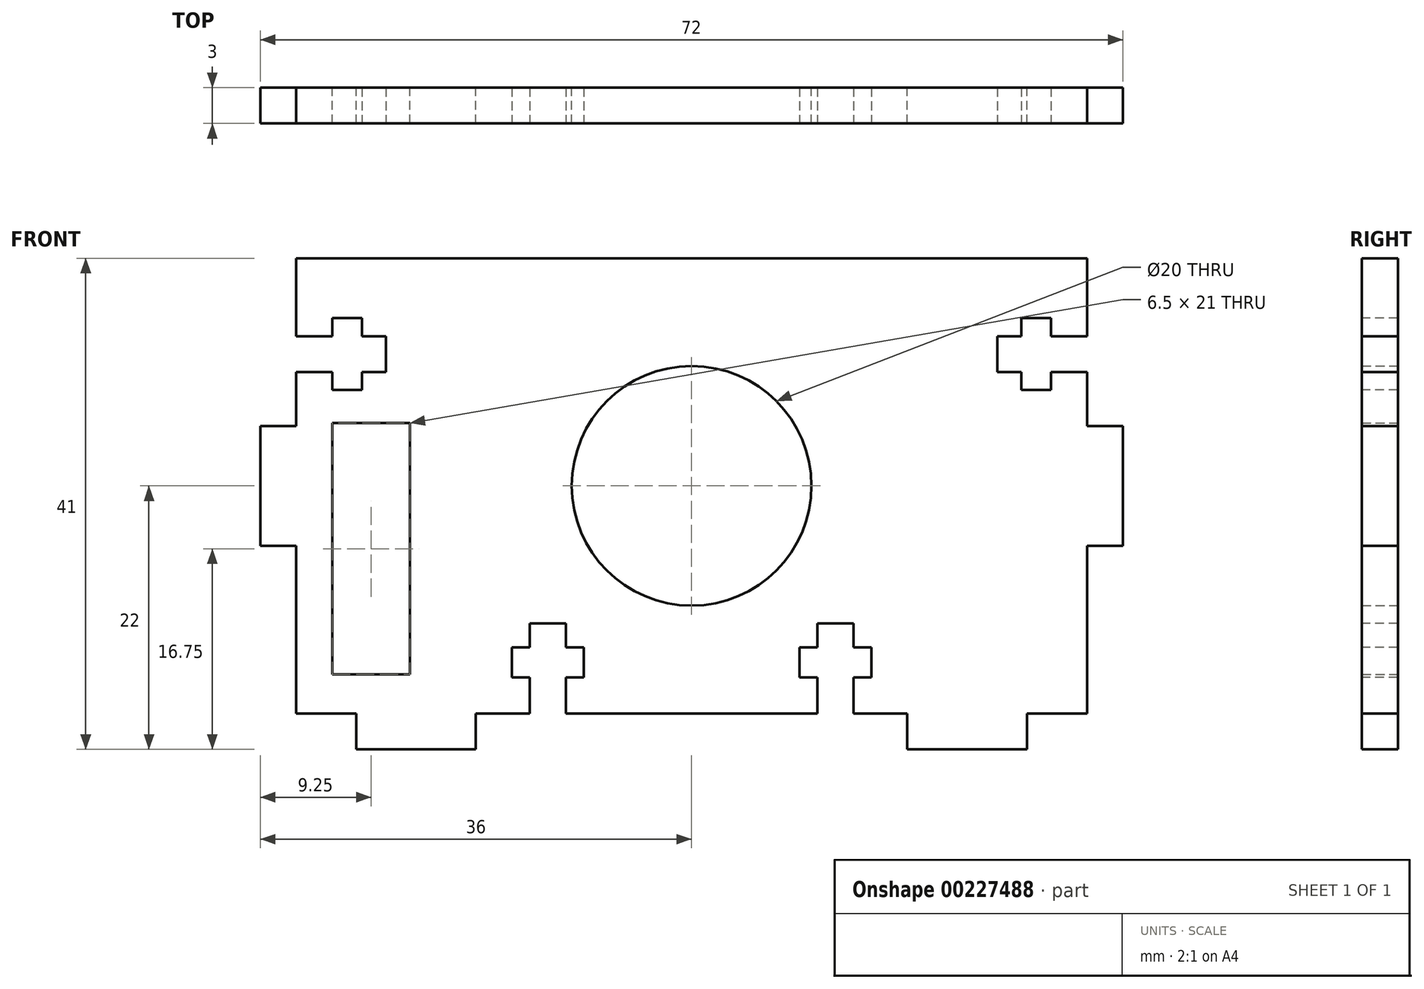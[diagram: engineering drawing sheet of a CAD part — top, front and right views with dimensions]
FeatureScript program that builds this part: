
annotation { "Feature Type Name" : "Feature", "Feature Type Description" : "" }
export const myFeature = defineFeature(function(context is Context, id is Id, definition is map)
    precondition{}
    {
        {
            var Q0;
            Q0=qCreatedBy(makeId("Front.planeOp"),FACE);
            var sketch = newSketch(context, id + "F0", { "sketchPlane" : qUnion([Q0])});
            skLineSegment(sketch, "E0.top", {"start": v(33, 19) * mm, "end": v(-33, 19) * mm});
            skPoint(sketch, "E0.middle", {"position": v(0, 0) * mm});
            skCircle(sketch, "E1", {"center": v(0, 0) * mm, "radius": 10 * mm});
            skPoint(sketch, "E2", {"position": v(0, 19) * mm});
            skLineSegment(sketch, "E3", {"start": v(-28, -19) * mm, "end": v(-28, -22) * mm});
            skLineSegment(sketch, "E4", {"start": v(-28, -22) * mm, "end": v(-18, -22) * mm});
            skLineSegment(sketch, "E5", {"start": v(-18, -22) * mm, "end": v(-18, -19) * mm});
            skLineSegment(sketch, "E6", {"start": v(-18, -19) * mm, "end": v(0, -19) * mm});
            skLineSegment(sketch, "E7.MirrorCS", {"start": v(18, -19) * mm, "end": v(0, -19) * mm});
            skLineSegment(sketch, "E8.MirrorCS", {"start": v(18, -22) * mm, "end": v(18, -19) * mm});
            skLineSegment(sketch, "E9.MirrorCS", {"start": v(28, -22) * mm, "end": v(18, -22) * mm});
            skLineSegment(sketch, "E10.MirrorCS", {"start": v(28, -19) * mm, "end": v(28, -22) * mm});
            skLineSegment(sketch, "E11", {"start": v(-33, -19) * mm, "end": v(-33, -5) * mm});
            skLineSegment(sketch, "E12", {"start": v(-33, -5) * mm, "end": v(-36, -5) * mm});
            skLineSegment(sketch, "E13", {"start": v(-36, -5) * mm, "end": v(-36, 5) * mm});
            skLineSegment(sketch, "E14", {"start": v(-36, 5) * mm, "end": v(-33, 5) * mm});
            skLineSegment(sketch, "E15", {"start": v(-33, 5) * mm, "end": v(-33, 19) * mm});
            skPoint(sketch, "E16", {"position": v(-36, 0) * mm});
            skLineSegment(sketch, "E17.MirrorCS", {"start": v(33, 5) * mm, "end": v(33, 19) * mm});
            skLineSegment(sketch, "E18.MirrorCS", {"start": v(36, 5) * mm, "end": v(33, 5) * mm});
            skLineSegment(sketch, "E19.MirrorCS", {"start": v(36, -5) * mm, "end": v(36, 5) * mm});
            skLineSegment(sketch, "E20.MirrorCS", {"start": v(33, -5) * mm, "end": v(36, -5) * mm});
            skLineSegment(sketch, "E21.MirrorCS", {"start": v(33, -19) * mm, "end": v(33, -5) * mm});
            skLineSegment(sketch, "E22", {"start": v(28, -19) * mm, "end": v(33, -19) * mm});
            skLineSegment(sketch, "E23", {"start": v(-28, -19) * mm, "end": v(-33, -19) * mm});
            skLineSegment(sketch, "E24.bottom", {"start": v(-30, 5.25) * mm, "end": v(-23.5, 5.25) * mm});
            skLineSegment(sketch, "E24.top", {"start": v(-30, -15.75) * mm, "end": v(-23.5, -15.75) * mm});
            skLineSegment(sketch, "E24.left", {"start": v(-30, 5.25) * mm, "end": v(-30, -15.75) * mm});
            skLineSegment(sketch, "E24.right", {"start": v(-23.5, 5.25) * mm, "end": v(-23.5, -15.75) * mm});
            skSolve(sketch);
        }
        {
            var Q0;
            Q0=makeQuery(id+"F0.imprint","IMPRINT",FACE,{"disambiguationData":[TD([[makeQuery(id+"F0.imprint","IMPRINT",EDGE,{"derivedFrom":sQuery(id+"F0.wireOp",EDGE,"E0.bottom")}),-1.0]])]});
            var Q1;
            Q1=makeQuery(id+"F0.imprint","IMPRINT",FACE,{"disambiguationData":[TD([[makeQuery(id+"F0.imprint","IMPRINT",EDGE,{"derivedFrom":sQuery(id+"F0.wireOp",EDGE,"E0.top")}),1.0]])]});
            extrude(context, id + "F1", {"entities" : qUnion([Q0, Q1]), "depth" : 3 * mm});
        }
        {
            var Q0;
            Q0=makeQuery(id+"F1.opExtrude","CAP_FACE",FACE,{"disambiguationData":[OSD([sQuery(id+"F0.wireOp",EDGE,"E0.top"),sQuery(id+"F0.wireOp",EDGE,"E1"),sQuery(id+"F0.wireOp",EDGE,"i2BJ4We7-Z1tz-6YYD-7Gnh-UwGsJDHukj4o"),sQuery(id+"F0.wireOp",EDGE,"H5TLaSxA-TAvm-WxYI-6s5p-rbUKsHJPtpz8"),sQuery(id+"F0.wireOp",EDGE,"fE5sAuBm-J1N4-LUQK-MxoP-oJGd3h4EWBky"),sQuery(id+"F0.wireOp",EDGE,"UVkaeSOW-HMeC-MlRq-fWxO-58zO0Vm4gzLd"),sQuery(id+"F0.wireOp",EDGE,"4oAcHBtJ-SWL1-Us38-5a5N-tiTYXxMsnVxl"),sQuery(id+"F0.wireOp",EDGE,"MGHFterx-abw6-INuc-nvHV-QaNsLm6ah1ng"),sQuery(id+"F0.wireOp",EDGE,"DztduCwT-NtgE-rZnK-mSEW-EnSqVKOmk10X"),sQuery(id+"F0.wireOp",EDGE,"XImseshz-UxQT-ogDy-5Lvy-O5B2oz8zv5fS"),sQuery(id+"F0.wireOp",EDGE,"FHz1HeJZ-Y50a-yfiC-Rnzm-b0fU7RSFoIpM"),sQuery(id+"F0.wireOp",EDGE,"bBcTDBjg-FDSx-XcTB-SbE1-9syf6QqrHLmC"),sQuery(id+"F0.wireOp",EDGE,"1vXtDNT1-yAZY-NYDk-InIM-wFA5S2rVquaF"),sQuery(id+"F0.wireOp",EDGE,"rcTIoJpC-EadT-N3WT-61kg-b3dVzh2UPf16"),sQuery(id+"F0.wireOp",EDGE,"V9EOst0m-YofT-ZeQ4-KXmd-etc1AHxpQRv2"),sQuery(id+"F0.wireOp",EDGE,"E3"),sQuery(id+"F0.wireOp",EDGE,"E4"),sQuery(id+"F0.wireOp",EDGE,"E5"),sQuery(id+"F0.wireOp",EDGE,"E6"),sQuery(id+"F0.wireOp",EDGE,"E7.MirrorCS"),sQuery(id+"F0.wireOp",EDGE,"E8.MirrorCS"),sQuery(id+"F0.wireOp",EDGE,"E9.MirrorCS"),sQuery(id+"F0.wireOp",EDGE,"E10.MirrorCS"),sQuery(id+"F0.wireOp",EDGE,"4fc586d0-1a2d-4033-9ad1-b4b14924f1e60.MirrorCS"),sQuery(id+"F0.wireOp",EDGE,"25921314-2feb-4960-9358-c6f40c29e8060.MirrorCS"),sQuery(id+"F0.wireOp",EDGE,"92609e8c-4cca-44cb-b192-d1e8ea80d6400.MirrorCS"),sQuery(id+"F0.wireOp",EDGE,"c6435143-3ef5-4a16-a53c-0c7a1f294e250.MirrorCS"),sQuery(id+"F0.wireOp",EDGE,"302a1fd6-7f51-4dcd-b85b-b87c70c5ff6f0.MirrorCS"),sQuery(id+"F0.wireOp",EDGE,"271ff51f-9e70-48b1-9ca4-6ffa4ba6ee090.MirrorCS"),sQuery(id+"F0.wireOp",EDGE,"7c8ad784-0027-4aca-88da-cb9512f49f770.MirrorCS"),sQuery(id+"F0.wireOp",EDGE,"aab8c399-5e78-4643-9a76-05bc1427fb740.MirrorCS"),sQuery(id+"F0.wireOp",EDGE,"2a5f69ab-9c37-4cf4-a27a-83d52b59f34f0.MirrorCS"),sQuery(id+"F0.wireOp",EDGE,"8a72d888-9ff6-4074-9ea7-52382edc54d80.MirrorCS"),sQuery(id+"F0.wireOp",EDGE,"2b144515-558f-4b7e-bfd9-8a7150f656b50.MirrorCS"),sQuery(id+"F0.wireOp",EDGE,"7271def4-b984-4847-8607-e135956054630.MirrorCS"),sQuery(id+"F0.wireOp",EDGE,"d1406031-9f0b-476a-854e-e83de3dd73970.MirrorCS"),sQuery(id+"F0.wireOp",EDGE,"0yL6zwbu-xF7a-lJXO-zZG0-wwet5oho1wIb"),sQuery(id+"F0.wireOp",EDGE,"46feee59-1b5a-4064-8cc5-d9cbb5a2c9400.MirrorC"),sQuery(id+"F0.wireOp",EDGE,"E11"),sQuery(id+"F0.wireOp",EDGE,"E12"),sQuery(id+"F0.wireOp",EDGE,"E13"),sQuery(id+"F0.wireOp",EDGE,"E14"),sQuery(id+"F0.wireOp",EDGE,"E15"),sQuery(id+"F0.wireOp",EDGE,"E17.MirrorCS"),sQuery(id+"F0.wireOp",EDGE,"E18.MirrorCS"),sQuery(id+"F0.wireOp",EDGE,"E19.MirrorCS"),sQuery(id+"F0.wireOp",EDGE,"E20.MirrorCS"),sQuery(id+"F0.wireOp",EDGE,"E21.MirrorCS")])],"isStart":false});
            var sketch = newSketch(context, id + "F2", { "sketchPlane" : qUnion([Q0])});
            skLineSegment(sketch, "E25", {"start": v(10.5, -19) * mm, "end": v(10.5, -16) * mm});
            skLineSegment(sketch, "E26", {"start": v(10.5, -16) * mm, "end": v(9, -16) * mm});
            skLineSegment(sketch, "E27", {"start": v(9, -16) * mm, "end": v(9, -13.5) * mm});
            skLineSegment(sketch, "E28", {"start": v(9, -13.5) * mm, "end": v(10.5, -13.5) * mm});
            skLineSegment(sketch, "E29", {"start": v(10.5, -13.5) * mm, "end": v(10.5, -11.5) * mm});
            skLineSegment(sketch, "E30", {"start": v(10.5, -11.5) * mm, "end": v(13.5, -11.5) * mm});
            skLineSegment(sketch, "E31", {"start": v(13.5, -11.5) * mm, "end": v(13.5, -13.5) * mm});
            skLineSegment(sketch, "E32", {"start": v(13.5, -13.5) * mm, "end": v(15, -13.5) * mm});
            skLineSegment(sketch, "E33", {"start": v(15, -13.5) * mm, "end": v(15, -16) * mm});
            skLineSegment(sketch, "E34", {"start": v(15, -16) * mm, "end": v(13.5, -16) * mm});
            skLineSegment(sketch, "E35", {"start": v(13.5, -16) * mm, "end": v(13.5, -19) * mm});
            skPoint(sketch, "E36", {"position": v(12, -19) * mm});
            skLineSegment(sketch, "E37", {"start": v(13.5, -19) * mm, "end": v(10.5, -19) * mm});
            skLineSegment(sketch, "E38", {"start": v(33, 9.5) * mm, "end": v(30, 9.5) * mm});
            skLineSegment(sketch, "E39", {"start": v(30, 9.5) * mm, "end": v(30, 8) * mm});
            skLineSegment(sketch, "E40", {"start": v(30, 8) * mm, "end": v(27.5, 8) * mm});
            skLineSegment(sketch, "E41", {"start": v(27.5, 8) * mm, "end": v(27.5, 9.5) * mm});
            skLineSegment(sketch, "E42", {"start": v(27.5, 9.5) * mm, "end": v(25.5, 9.5) * mm});
            skLineSegment(sketch, "E43", {"start": v(25.5, 9.5) * mm, "end": v(25.5, 12.5) * mm});
            skLineSegment(sketch, "E44", {"start": v(25.5, 12.5) * mm, "end": v(27.5, 12.5) * mm});
            skLineSegment(sketch, "E45", {"start": v(27.5, 12.5) * mm, "end": v(27.5, 14) * mm});
            skLineSegment(sketch, "E46", {"start": v(27.5, 14) * mm, "end": v(30, 14) * mm});
            skLineSegment(sketch, "E47", {"start": v(30, 14) * mm, "end": v(30, 12.5) * mm});
            skLineSegment(sketch, "E48", {"start": v(30, 12.5) * mm, "end": v(33, 12.5) * mm});
            skPoint(sketch, "E49", {"position": v(33, 11) * mm});
            skLineSegment(sketch, "E50", {"start": v(33, 12.5) * mm, "end": v(33, 9.5) * mm});
            skLineSegment(sketch, "E51.MirrorCS", {"start": v(-30, 14) * mm, "end": v(-30, 12.5) * mm});
            skLineSegment(sketch, "E52.MirrorCS", {"start": v(-33, 12.5) * mm, "end": v(-33, 9.5) * mm});
            skLineSegment(sketch, "E53.MirrorCS", {"start": v(-27.5, 8) * mm, "end": v(-27.5, 9.5) * mm});
            skLineSegment(sketch, "E54.MirrorCS", {"start": v(-27.5, 12.5) * mm, "end": v(-27.5, 14) * mm});
            skLineSegment(sketch, "E55.MirrorCS", {"start": v(-30, 9.5) * mm, "end": v(-30, 8) * mm});
            skPoint(sketch, "E56.MirrorP", {"position": v(-33, 11) * mm});
            skLineSegment(sketch, "E57.MirrorCS", {"start": v(-27.5, 9.5) * mm, "end": v(-25.5, 9.5) * mm});
            skLineSegment(sketch, "E58.MirrorCS", {"start": v(-33, 9.5) * mm, "end": v(-30, 9.5) * mm});
            skLineSegment(sketch, "E59.MirrorCS", {"start": v(-25.5, 12.5) * mm, "end": v(-27.5, 12.5) * mm});
            skLineSegment(sketch, "E60.MirrorCS", {"start": v(-30, 12.5) * mm, "end": v(-33, 12.5) * mm});
            skLineSegment(sketch, "E61.MirrorCS", {"start": v(-27.5, 14) * mm, "end": v(-30, 14) * mm});
            skLineSegment(sketch, "E62.MirrorCS", {"start": v(-30, 8) * mm, "end": v(-27.5, 8) * mm});
            skLineSegment(sketch, "E63.MirrorCS", {"start": v(-25.5, 9.5) * mm, "end": v(-25.5, 12.5) * mm});
            skLineSegment(sketch, "E64.MirrorCS", {"start": v(-13.5, -13.5) * mm, "end": v(-15, -13.5) * mm});
            skLineSegment(sketch, "E65.MirrorCS", {"start": v(-10.5, -16) * mm, "end": v(-9, -16) * mm});
            skLineSegment(sketch, "E66.MirrorCS", {"start": v(-15, -16) * mm, "end": v(-13.5, -16) * mm});
            skLineSegment(sketch, "E67.MirrorCS", {"start": v(-9, -13.5) * mm, "end": v(-10.5, -13.5) * mm});
            skLineSegment(sketch, "E68.MirrorCS", {"start": v(-13.5, -19) * mm, "end": v(-10.5, -19) * mm});
            skLineSegment(sketch, "E69.MirrorCS", {"start": v(-10.5, -13.5) * mm, "end": v(-10.5, -11.5) * mm});
            skLineSegment(sketch, "E70.MirrorCS", {"start": v(-13.5, -16) * mm, "end": v(-13.5, -19) * mm});
            skLineSegment(sketch, "E71.MirrorCS", {"start": v(-15, -13.5) * mm, "end": v(-15, -16) * mm});
            skLineSegment(sketch, "E72.MirrorCS", {"start": v(-9, -16) * mm, "end": v(-9, -13.5) * mm});
            skLineSegment(sketch, "E73.MirrorCS", {"start": v(-10.5, -19) * mm, "end": v(-10.5, -16) * mm});
            skLineSegment(sketch, "E74.MirrorCS", {"start": v(-10.5, -11.5) * mm, "end": v(-13.5, -11.5) * mm});
            skPoint(sketch, "E75.MirrorP", {"position": v(-12, -19) * mm});
            skLineSegment(sketch, "E76.MirrorCS", {"start": v(-13.5, -11.5) * mm, "end": v(-13.5, -13.5) * mm});
            skSolve(sketch);
        }
        {
            var Q0;
            Q0=makeQuery(id+"F2.imprint","IMPRINT",FACE,{"disambiguationData":[TD([[makeQuery(id+"F2.imprint","IMPRINT",EDGE,{"derivedFrom":sQuery(id+"F2.wireOp",EDGE,"e02e0eb0-34da-40b5-a29d-7ce47544084a.MirrorCS")}),1.0]])]});
            var Q1;
            Q1=makeQuery(id+"F2.imprint","IMPRINT",FACE,{"disambiguationData":[TD([[makeQuery(id+"F2.imprint","IMPRINT",EDGE,{"derivedFrom":sQuery(id+"F2.wireOp",EDGE,"E25")}),-1.0]])]});
            var Q2;
            Q2=makeQuery(id+"F2.imprint","IMPRINT",FACE,{"disambiguationData":[TD([[makeQuery(id+"F2.imprint","IMPRINT",EDGE,{"derivedFrom":sQuery(id+"F2.wireOp",EDGE,"E38")}),-1.0]])]});
            var Q3;
            Q3=makeQuery(id+"F2.imprint","IMPRINT",FACE,{"disambiguationData":[TD([[makeQuery(id+"F2.imprint","IMPRINT",EDGE,{"derivedFrom":sQuery(id+"F2.wireOp",EDGE,"E51.MirrorCS")}),1.0]])]});
            var Q4;
            Q4=makeQuery(id+"F2.imprint","IMPRINT",FACE,{"disambiguationData":[TD([[makeQuery(id+"F2.imprint","IMPRINT",EDGE,{"derivedFrom":sQuery(id+"F2.wireOp",EDGE,"E64.MirrorCS")}),1.0]])]});
            var Q5;
            Q5=makeQuery(id+"F2.imprint","IMPRINT",FACE,{"disambiguationData":[TD([[makeQuery(id+"F2.imprint","IMPRINT",EDGE,{"derivedFrom":sQuery(id+"F2.wireOp",EDGE,"j8ZFTuHN-Sw0p-I60I-krbt-rPzmva6GH3Ty.bottom")}),-1.0]])]});
            extrude(context, id + "F3", {"entities" : qUnion([Q0, Q1, Q2, Q3, Q4, Q5]), "operationType" : NewBodyOperationType.REMOVE, "endBound" : BoundingType.UP_TO_NEXT, "oppositeDirection" : true, "depth" : 25 * mm});
        }
    });
